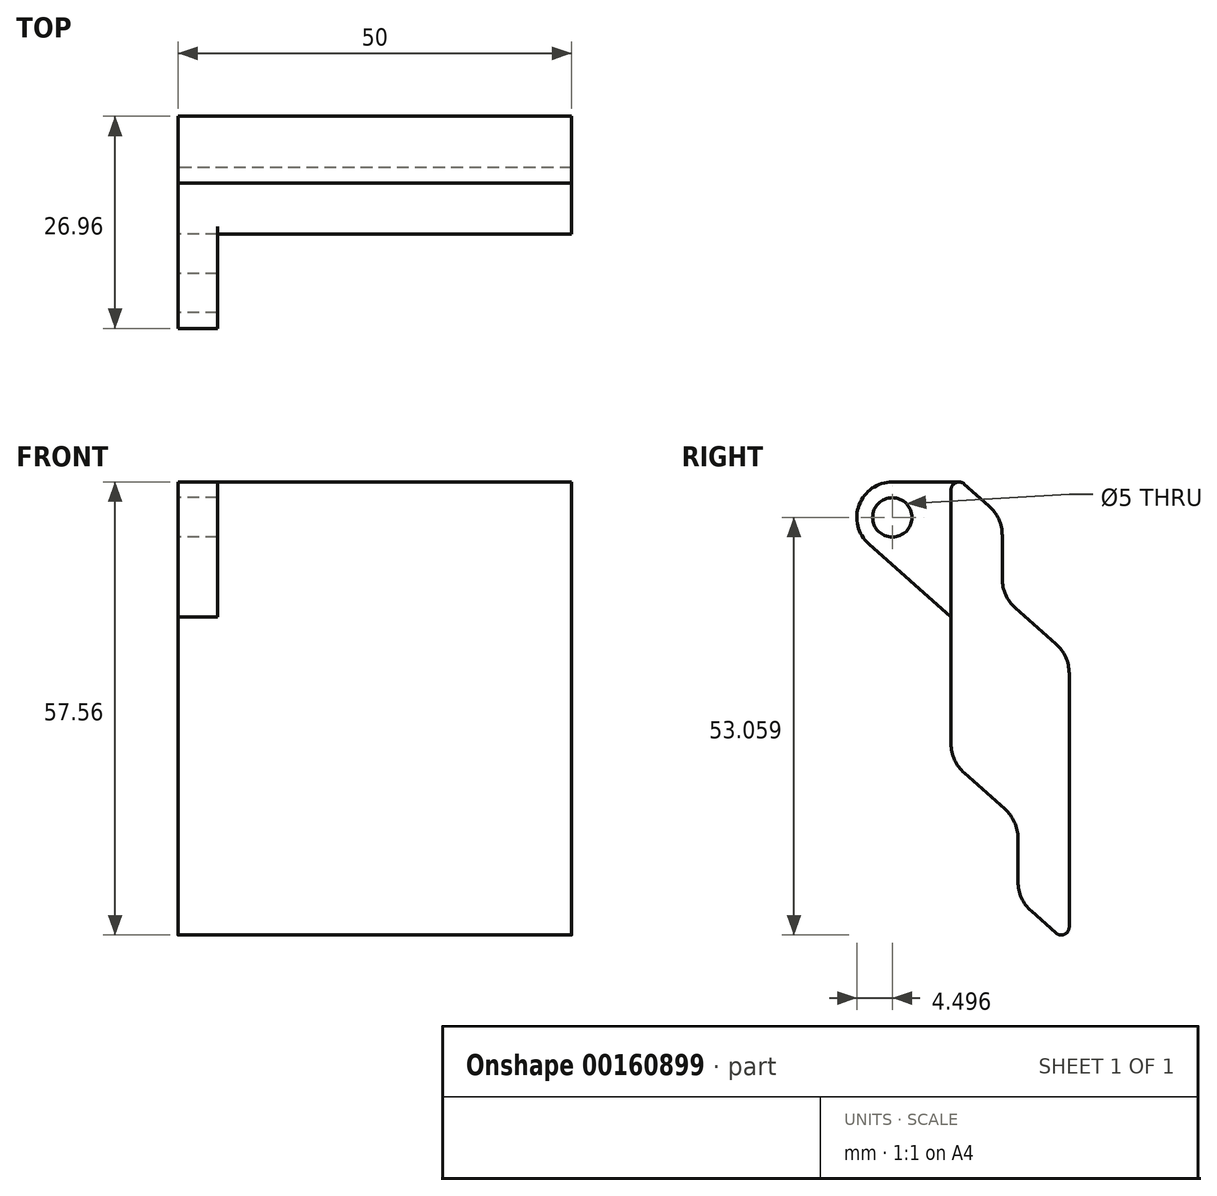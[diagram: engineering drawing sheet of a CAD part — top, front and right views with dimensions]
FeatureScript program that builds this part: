
annotation { "Feature Type Name" : "Feature", "Feature Type Description" : "" }
export const myFeature = defineFeature(function(context is Context, id is Id, definition is map)
    precondition{}
    {
        {
            var Q0;
            Q0=qCreatedBy(makeId("Right.planeOp"),FACE);
            var sketch = newSketch(context, id + "F0", { "sketchPlane" : qUnion([Q0])});
            skLineSegment(sketch, "E0.left", {"start": v(7.5, -27.78) * mm, "end": v(7.5, 4.46) * mm});
            skLineSegment(sketch, "E0.right", {"start": v(-7.5, -4.46) * mm, "end": v(-7.5, 27.78) * mm});
            skPoint(sketch, "E0.middle", {"position": v(0, 0) * mm});
            skLineSegment(sketch, "E1", {"start": v(-1, 22) * mm, "end": v(-1, 16.5) * mm});
            skLineSegment(sketch, "E2", {"start": v(0.69, 12.75) * mm, "end": v(5.81, 8.2) * mm});
            skLineSegment(sketch, "E3", {"start": v(-5.81, -8.2) * mm, "end": v(-0.69, -12.75) * mm});
            skLineSegment(sketch, "E4", {"start": v(1, -16.5) * mm, "end": v(1, -22) * mm});
            skLineSegment(sketch, "E5", {"start": v(-5.84, 28.53) * mm, "end": v(-2.69, 25.74) * mm});
            skLineSegment(sketch, "E6", {"start": v(2.69, -25.74) * mm, "end": v(5.84, -28.53) * mm});
            skCircle(sketch, "E7", {"center": v(0, 0) * mm, "radius": 10 * mm, "construction": true});
            skPoint(sketch, "E8.visualSharp", {"position": v(-1, 24.24) * mm});
            skArc(sketch, "E8.filletArc", {"start": v(-1, 22) * mm, "mid": v(-1.44, 24.05) * mm, "end": v(-2.69, 25.74) * mm});
            skPoint(sketch, "E9.visualSharp", {"position": v(-1, 14.24) * mm});
            skArc(sketch, "E9.filletArc", {"start": v(-1, 16.5) * mm, "mid": v(-0.56, 14.44) * mm, "end": v(0.69, 12.75) * mm});
            skPoint(sketch, "E10.visualSharp", {"position": v(1, -14.24) * mm});
            skArc(sketch, "E10.filletArc", {"start": v(1, -16.5) * mm, "mid": v(0.56, -14.44) * mm, "end": v(-0.69, -12.75) * mm});
            skPoint(sketch, "E11.visualSharp", {"position": v(-7.5, -6.72) * mm});
            skArc(sketch, "E11.filletArc", {"start": v(-7.5, -4.46) * mm, "mid": v(-7.06, -6.52) * mm, "end": v(-5.81, -8.2) * mm});
            skPoint(sketch, "E12.visualSharp", {"position": v(1, -24.24) * mm});
            skArc(sketch, "E12.filletArc", {"start": v(1, -22) * mm, "mid": v(1.44, -24.05) * mm, "end": v(2.69, -25.74) * mm});
            skPoint(sketch, "E13.visualSharp", {"position": v(7.5, 6.72) * mm});
            skArc(sketch, "E13.filletArc", {"start": v(7.5, 4.46) * mm, "mid": v(7.06, 6.52) * mm, "end": v(5.81, 8.2) * mm});
            skPoint(sketch, "E14.visualSharp", {"position": v(-7.5, 30) * mm});
            skArc(sketch, "E14.filletArc", {"start": v(-5.84, 28.53) * mm, "mid": v(-6.91, 28.7) * mm, "end": v(-7.5, 27.78) * mm});
            skPoint(sketch, "E15.visualSharp", {"position": v(7.5, -30) * mm});
            skArc(sketch, "E15.filletArc", {"start": v(5.84, -28.53) * mm, "mid": v(6.91, -28.7) * mm, "end": v(7.5, -27.78) * mm});
            skSolve(sketch);
        }
        {
            var Q0;
            Q0=makeQuery(id+"F0.imprint","IMPRINT",FACE,{"disambiguationData":[TD([[makeQuery(id+"F0.imprint","IMPRINT",EDGE,{"derivedFrom":sQuery(id+"F0.wireOp",EDGE,"E0.left")}),1.0]])]});
            extrude(context, id + "F1", {"entities" : qUnion([Q0]), "endBound" : BoundingType.SYMMETRIC, "depth" : 50 * mm});
        }
        {
            var Q0;
            Q0=makeQuery(id+"F1.opExtrude","CAP_FACE",FACE,{"disambiguationData":[OSD([sQuery(id+"F0.wireOp",EDGE,"E0.left"),sQuery(id+"F0.wireOp",EDGE,"E0.right"),sQuery(id+"F0.wireOp",EDGE,"E1"),sQuery(id+"F0.wireOp",EDGE,"E2"),sQuery(id+"F0.wireOp",EDGE,"E3"),sQuery(id+"F0.wireOp",EDGE,"E4"),sQuery(id+"F0.wireOp",EDGE,"E5"),sQuery(id+"F0.wireOp",EDGE,"E6"),sQuery(id+"F0.wireOp",EDGE,"E8.filletArc"),sQuery(id+"F0.wireOp",EDGE,"E9.filletArc"),sQuery(id+"F0.wireOp",EDGE,"E10.filletArc"),sQuery(id+"F0.wireOp",EDGE,"E11.filletArc"),sQuery(id+"F0.wireOp",EDGE,"E12.filletArc"),sQuery(id+"F0.wireOp",EDGE,"E13.filletArc"),sQuery(id+"F0.wireOp",EDGE,"E14.filletArc"),sQuery(id+"F0.wireOp",EDGE,"E15.filletArc")])],"isStart":true});
            var sketch = newSketch(context, id + "F2", { "sketchPlane" : qUnion([Q0])});
            skCircle(sketch, "E16", {"center": v(14.96, 24.28) * mm, "radius": 2.5 * mm});
            skArc(sketch, "E17", {"start": v(17.95, 20.9) * mm, "mid": v(19.17, 25.87) * mm, "end": v(14.96, 28.78) * mm});
            skLineSegment(sketch, "E18", {"start": v(17.95, 20.9) * mm, "end": v(7.5, 11.66) * mm});
            skLineSegment(sketch, "E19", {"start": v(14.96, 28.78) * mm, "end": v(6.5, 28.78) * mm});
            skSolve(sketch);
        }
        {
            var Q0;
            Q0=makeQuery(id+"F2.imprint","IMPRINT",FACE,{"disambiguationData":[TD([[makeQuery(id+"F2.imprint","IMPRINT",EDGE,{"derivedFrom":sQuery(id+"F2.wireOp",EDGE,"E16")}),-1.0]])]});
            extrude(context, id + "F3", {"entities" : qUnion([Q0]), "operationType" : NewBodyOperationType.ADD, "oppositeDirection" : true, "depth" : 5 * mm});
        }
    });
